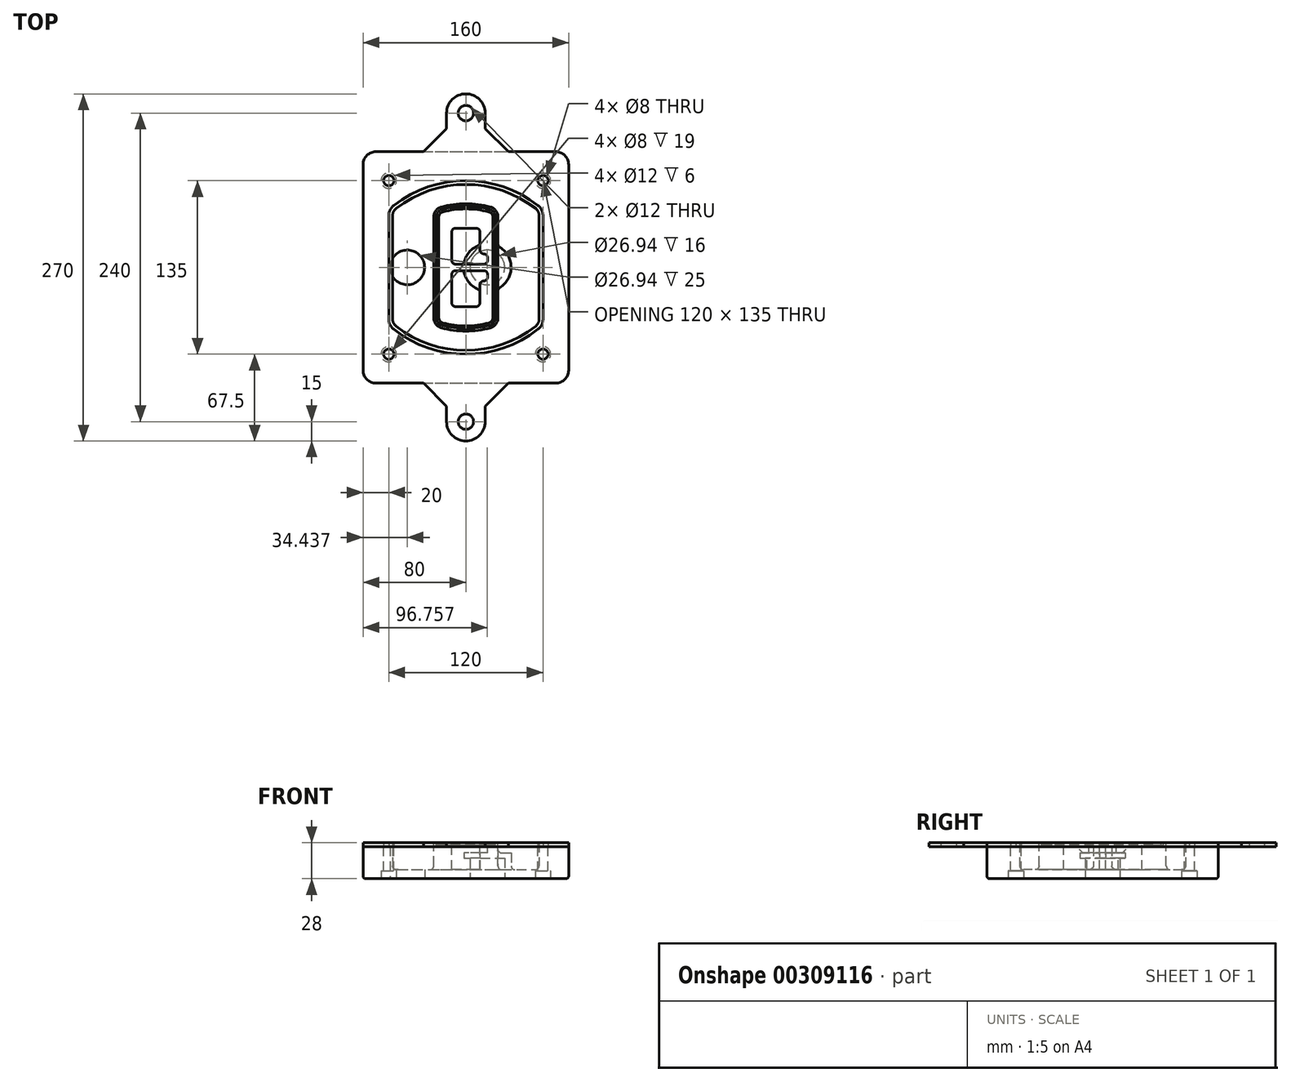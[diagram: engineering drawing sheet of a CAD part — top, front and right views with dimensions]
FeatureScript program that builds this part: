
annotation { "Feature Type Name" : "Feature", "Feature Type Description" : "" }
export const myFeature = defineFeature(function(context is Context, id is Id, definition is map)
    precondition{}
    {
        {
            var Q0;
            Q0=qCreatedBy(makeId("Top.planeOp"),FACE);
            var sketch = newSketch(context, id + "F0", { "sketchPlane" : qUnion([Q0])});
            skPoint(sketch, "E0.rect.middle", {"position": v(0, 0) * mm});
            skLineSegment(sketch, "E1.bottom", {"start": v(-70, -90) * mm, "end": v(70, -90) * mm});
            skLineSegment(sketch, "E1.top", {"start": v(-70, 90) * mm, "end": v(70, 90) * mm});
            skLineSegment(sketch, "E1.left", {"start": v(-80, -80) * mm, "end": v(-80, 80) * mm});
            skLineSegment(sketch, "E1.right", {"start": v(80, -80) * mm, "end": v(80, 80) * mm});
            skLineSegment(sketch, "E2", {"start": v(-80, 90) * mm, "end": v(80, -90) * mm, "construction": true});
            skLineSegment(sketch, "E3", {"start": v(80, 90) * mm, "end": v(-80, -90) * mm, "construction": true});
            skCircle(sketch, "E4", {"center": v(-60, 67.5) * mm, "radius": 4 * mm});
            skCircle(sketch, "E5", {"center": v(60, 67.5) * mm, "radius": 4 * mm});
            skCircle(sketch, "E6", {"center": v(60, -67.5) * mm, "radius": 4 * mm});
            skCircle(sketch, "E7", {"center": v(-60, -67.5) * mm, "radius": 4 * mm});
            skLineSegment(sketch, "E8", {"start": v(-60, 67.5) * mm, "end": v(60, 67.5) * mm, "construction": true});
            skLineSegment(sketch, "E9", {"start": v(60, 67.5) * mm, "end": v(60, -67.5) * mm, "construction": true});
            skLineSegment(sketch, "E10", {"start": v(60, -67.5) * mm, "end": v(-60, -67.5) * mm, "construction": true});
            skLineSegment(sketch, "E11", {"start": v(-60, -67.5) * mm, "end": v(-60, 67.5) * mm, "construction": true});
            skLineSegment(sketch, "E12", {"start": v(-60, 40.3) * mm, "end": v(-60, -40.3) * mm});
            skLineSegment(sketch, "E13", {"start": v(60, 40.3) * mm, "end": v(60, -40.3) * mm});
            skArc(sketch, "E14", {"start": v(56.15, 48.18) * mm, "mid": v(0, 67.5) * mm, "end": v(-56.15, 48.18) * mm});
            skArc(sketch, "E15", {"start": v(-56.15, -48.18) * mm, "mid": v(0, -67.5) * mm, "end": v(56.15, -48.18) * mm});
            skLineSegment(sketch, "E16", {"start": v(-60, 0) * mm, "end": v(60, 0) * mm, "construction": true});
            skPoint(sketch, "E17.visualSharp", {"position": v(-60, -45) * mm});
            skArc(sketch, "E17.filletArc", {"start": v(-60, -40.3) * mm, "mid": v(-58.99, -44.68) * mm, "end": v(-56.15, -48.18) * mm});
            skPoint(sketch, "E18.visualSharp", {"position": v(-60, 45) * mm});
            skArc(sketch, "E18.filletArc", {"start": v(-56.15, 48.18) * mm, "mid": v(-58.99, 44.68) * mm, "end": v(-60, 40.3) * mm});
            skPoint(sketch, "E19.visualSharp", {"position": v(60, 45) * mm});
            skArc(sketch, "E19.filletArc", {"start": v(60, 40.3) * mm, "mid": v(58.99, 44.68) * mm, "end": v(56.15, 48.18) * mm});
            skPoint(sketch, "E20.visualSharp", {"position": v(60, -45) * mm});
            skArc(sketch, "E20.filletArc", {"start": v(56.15, -48.18) * mm, "mid": v(58.99, -44.68) * mm, "end": v(60, -40.3) * mm});
            skPoint(sketch, "E21.visualSharp", {"position": v(-80, 90) * mm});
            skArc(sketch, "E21.filletArc", {"start": v(-70, 90) * mm, "mid": v(-77.07, 87.07) * mm, "end": v(-80, 80) * mm});
            skPoint(sketch, "E22.visualSharp", {"position": v(80, 90) * mm});
            skArc(sketch, "E22.filletArc", {"start": v(80, 80) * mm, "mid": v(77.07, 87.07) * mm, "end": v(70, 90) * mm});
            skPoint(sketch, "E23.visualSharp", {"position": v(80, -90) * mm});
            skArc(sketch, "E23.filletArc", {"start": v(70, -90) * mm, "mid": v(77.07, -87.07) * mm, "end": v(80, -80) * mm});
            skPoint(sketch, "E24.visualSharp", {"position": v(-80, -90) * mm});
            skArc(sketch, "E24.filletArc", {"start": v(-80, -80) * mm, "mid": v(-77.07, -87.07) * mm, "end": v(-70, -90) * mm});
            skArc(sketch, "E25.0", {"start": v(57, 40.3) * mm, "mid": v(56.3, 43.36) * mm, "end": v(54.3, 45.81) * mm});
            skLineSegment(sketch, "E25.1", {"start": v(57, 40.3) * mm, "end": v(57, -40.3) * mm});
            skArc(sketch, "E25.2", {"start": v(54.3, -45.81) * mm, "mid": v(56.3, -43.36) * mm, "end": v(57, -40.3) * mm});
            skArc(sketch, "E25.3", {"start": v(-54.3, -45.81) * mm, "mid": v(0, -64.5) * mm, "end": v(54.3, -45.81) * mm});
            skArc(sketch, "E25.4", {"start": v(-57, -40.3) * mm, "mid": v(-56.3, -43.36) * mm, "end": v(-54.3, -45.81) * mm});
            skArc(sketch, "E25.5", {"start": v(54.3, 45.81) * mm, "mid": v(0, 64.5) * mm, "end": v(-54.3, 45.81) * mm});
            skLineSegment(sketch, "E25.6", {"start": v(-57, 40.3) * mm, "end": v(-57, -40.3) * mm});
            skArc(sketch, "E25.7", {"start": v(-54.3, 45.81) * mm, "mid": v(-56.3, 43.36) * mm, "end": v(-57, 40.3) * mm});
            skArc(sketch, "E26.0", {"start": v(-58.62, 51.33) * mm, "mid": v(-62.58, 46.43) * mm, "end": v(-64, 40.3) * mm});
            skArc(sketch, "E26.1", {"start": v(58.62, 51.33) * mm, "mid": v(0, 71.5) * mm, "end": v(-58.62, 51.33) * mm});
            skArc(sketch, "E26.2", {"start": v(64, 40.3) * mm, "mid": v(62.58, 46.43) * mm, "end": v(58.62, 51.33) * mm});
            skLineSegment(sketch, "E26.3", {"start": v(64, 40.3) * mm, "end": v(64, -40.3) * mm});
            skArc(sketch, "E26.4", {"start": v(58.62, -51.33) * mm, "mid": v(62.58, -46.43) * mm, "end": v(64, -40.3) * mm});
            skLineSegment(sketch, "E26.5", {"start": v(-64, 40.3) * mm, "end": v(-64, -40.3) * mm});
            skArc(sketch, "E26.6", {"start": v(-58.62, -51.33) * mm, "mid": v(0, -71.5) * mm, "end": v(58.62, -51.33) * mm});
            skArc(sketch, "E26.7", {"start": v(-64, -40.3) * mm, "mid": v(-62.58, -46.43) * mm, "end": v(-58.62, -51.33) * mm});
            skSolve(sketch);
        }
        {
            var Q0;
            Q0=makeQuery(id+"F0.imprint","IMPRINT",FACE,{"disambiguationData":[TD([[makeQuery(id+"F0.imprint","IMPRINT",EDGE,{"derivedFrom":sQuery(id+"F0.wireOp",EDGE,"E1.bottom")}),1.0]])]});
            var Q1;
            Q1=makeQuery(id+"F0.imprint","IMPRINT",FACE,{"disambiguationData":[TD([[makeQuery(id+"F0.imprint","IMPRINT",EDGE,{"derivedFrom":sQuery(id+"F0.wireOp",EDGE,"E12")}),1.0]])]});
            var Q2;
            Q2=makeQuery(id+"F0.imprint","IMPRINT",FACE,{"disambiguationData":[TD([[makeQuery(id+"F0.imprint","IMPRINT",EDGE,{"derivedFrom":sQuery(id+"F0.wireOp",EDGE,"E25.0")}),1.0]])]});
            var Q3;
            Q3=makeQuery(id+"F0.imprint","IMPRINT",FACE,{"disambiguationData":[TD([[makeQuery(id+"F0.imprint","IMPRINT",EDGE,{"derivedFrom":sQuery(id+"F0.wireOp",EDGE,"E12")}),-1.0]])]});
            extrude(context, id + "F1", {"entities" : qUnion([Q0, Q1, Q2, Q3]), "oppositeDirection" : true, "depth" : 25 * mm});
        }
        {
            var Q0;
            Q0=makeQuery(id+"F0.imprint","IMPRINT",FACE,{"disambiguationData":[TD([[makeQuery(id+"F0.imprint","IMPRINT",EDGE,{"derivedFrom":sQuery(id+"F0.wireOp",EDGE,"E12")}),1.0]])]});
            extrude(context, id + "F2", {"entities" : qUnion([Q0]), "operationType" : NewBodyOperationType.ADD, "depth" : 3 * mm});
        }
        {
            var Q0;
            Q0=makeQuery(id+"F0.imprint","IMPRINT",FACE,{"disambiguationData":[TD([[makeQuery(id+"F0.imprint","IMPRINT",EDGE,{"derivedFrom":sQuery(id+"F0.wireOp",EDGE,"E25.0")}),1.0]])]});
            extrude(context, id + "F3", {"entities" : qUnion([Q0]), "operationType" : NewBodyOperationType.REMOVE, "oppositeDirection" : true, "depth" : 18 * mm});
        }
        {
            var Q0;
            Q0=makeQuery(id+"F2.opExtrude","CAP_FACE",FACE,{"disambiguationData":[OSD([sQuery(id+"F0.wireOp",EDGE,"E12"),sQuery(id+"F0.wireOp",EDGE,"E13"),sQuery(id+"F0.wireOp",EDGE,"E14"),sQuery(id+"F0.wireOp",EDGE,"E15"),sQuery(id+"F0.wireOp",EDGE,"E17.filletArc"),sQuery(id+"F0.wireOp",EDGE,"E18.filletArc"),sQuery(id+"F0.wireOp",EDGE,"E19.filletArc"),sQuery(id+"F0.wireOp",EDGE,"E20.filletArc"),sQuery(id+"F0.wireOp",EDGE,"E25.0"),sQuery(id+"F0.wireOp",EDGE,"E25.1"),sQuery(id+"F0.wireOp",EDGE,"E25.2"),sQuery(id+"F0.wireOp",EDGE,"E25.3"),sQuery(id+"F0.wireOp",EDGE,"E25.4"),sQuery(id+"F0.wireOp",EDGE,"E25.5"),sQuery(id+"F0.wireOp",EDGE,"E25.6"),sQuery(id+"F0.wireOp",EDGE,"E25.7")])],"isStart":false});
            var sketch = newSketch(context, id + "F4", { "sketchPlane" : qUnion([Q0])});
            skArc(sketch, "E27.0", {"start": v(-19.08, -46.97) * mm, "mid": v(0, -49.5) * mm, "end": v(19.08, -46.97) * mm});
            skArc(sketch, "E28.0", {"start": v(19.08, 46.97) * mm, "mid": v(0, 49.5) * mm, "end": v(-19.08, 46.97) * mm});
            skLineSegment(sketch, "E29", {"start": v(-25, 39.25) * mm, "end": v(-25, -39.25) * mm});
            skLineSegment(sketch, "E30", {"start": v(25, 39.25) * mm, "end": v(25, -39.25) * mm});
            skLineSegment(sketch, "E31", {"start": v(-25, 45.1) * mm, "end": v(25, 45.1) * mm, "construction": true});
            skLineSegment(sketch, "E32", {"start": v(-25, -45.1) * mm, "end": v(25, -45.1) * mm, "construction": true});
            skPoint(sketch, "E33.visualSharp", {"position": v(-25, 45.1) * mm});
            skArc(sketch, "E33.filletArc", {"start": v(-19.08, 46.97) * mm, "mid": v(-23.35, 44.11) * mm, "end": v(-25, 39.25) * mm});
            skPoint(sketch, "E34.visualSharp", {"position": v(25, 45.1) * mm});
            skArc(sketch, "E34.filletArc", {"start": v(25, 39.25) * mm, "mid": v(23.35, 44.11) * mm, "end": v(19.08, 46.97) * mm});
            skPoint(sketch, "E35.visualSharp", {"position": v(25, -45.1) * mm});
            skArc(sketch, "E35.filletArc", {"start": v(19.08, -46.97) * mm, "mid": v(23.35, -44.11) * mm, "end": v(25, -39.25) * mm});
            skPoint(sketch, "E36.visualSharp", {"position": v(-25, -45.1) * mm});
            skArc(sketch, "E36.filletArc", {"start": v(-25, -39.25) * mm, "mid": v(-23.35, -44.11) * mm, "end": v(-19.08, -46.97) * mm});
            skArc(sketch, "E37.0", {"start": v(54.3, 45.81) * mm, "mid": v(0, 64.5) * mm, "end": v(-54.3, 45.81) * mm});
            skArc(sketch, "E37.1", {"start": v(-54.3, 45.81) * mm, "mid": v(-56.3, 43.36) * mm, "end": v(-57, 40.3) * mm});
            skLineSegment(sketch, "E37.2", {"start": v(-57, 40.3) * mm, "end": v(-57, -40.3) * mm});
            skArc(sketch, "E37.3", {"start": v(-57, -40.3) * mm, "mid": v(-56.3, -43.36) * mm, "end": v(-54.3, -45.81) * mm});
            skArc(sketch, "E37.4", {"start": v(-54.3, -45.81) * mm, "mid": v(0, -64.5) * mm, "end": v(54.3, -45.81) * mm});
            skArc(sketch, "E37.5", {"start": v(54.3, -45.81) * mm, "mid": v(56.3, -43.36) * mm, "end": v(57, -40.3) * mm});
            skLineSegment(sketch, "E37.6", {"start": v(57, 40.3) * mm, "end": v(57, -40.3) * mm});
            skArc(sketch, "E37.7", {"start": v(57, 40.3) * mm, "mid": v(56.3, 43.36) * mm, "end": v(54.3, 45.81) * mm});
            skLineSegment(sketch, "E38.0", {"start": v(23, 39.25) * mm, "end": v(23, -39.25) * mm});
            skArc(sketch, "E38.1", {"start": v(18.56, -45.04) * mm, "mid": v(21.76, -42.9) * mm, "end": v(23, -39.25) * mm});
            skArc(sketch, "E38.2", {"start": v(-18.56, -45.04) * mm, "mid": v(0, -47.5) * mm, "end": v(18.56, -45.04) * mm});
            skArc(sketch, "E38.3", {"start": v(-23, -39.25) * mm, "mid": v(-21.76, -42.9) * mm, "end": v(-18.56, -45.04) * mm});
            skLineSegment(sketch, "E38.4", {"start": v(-23, 39.25) * mm, "end": v(-23, -39.25) * mm});
            skArc(sketch, "E38.5", {"start": v(23, 39.25) * mm, "mid": v(21.76, 42.9) * mm, "end": v(18.56, 45.04) * mm});
            skArc(sketch, "E38.6", {"start": v(-18.56, 45.04) * mm, "mid": v(-21.76, 42.9) * mm, "end": v(-23, 39.25) * mm});
            skArc(sketch, "E38.7", {"start": v(18.56, 45.04) * mm, "mid": v(0, 47.5) * mm, "end": v(-18.56, 45.04) * mm});
            skArc(sketch, "E39.0", {"start": v(21, 39.25) * mm, "mid": v(20.18, 41.68) * mm, "end": v(18.04, 43.1) * mm});
            skLineSegment(sketch, "E39.1", {"start": v(21, 39.25) * mm, "end": v(21, -39.25) * mm});
            skArc(sketch, "E39.2", {"start": v(18.04, -43.1) * mm, "mid": v(20.18, -41.68) * mm, "end": v(21, -39.25) * mm});
            skArc(sketch, "E39.3", {"start": v(-18.04, -43.1) * mm, "mid": v(0, -45.5) * mm, "end": v(18.04, -43.1) * mm});
            skArc(sketch, "E39.4", {"start": v(-21, -39.25) * mm, "mid": v(-20.18, -41.68) * mm, "end": v(-18.04, -43.1) * mm});
            skArc(sketch, "E39.5", {"start": v(18.04, 43.1) * mm, "mid": v(0, 45.5) * mm, "end": v(-18.04, 43.1) * mm});
            skLineSegment(sketch, "E39.6", {"start": v(-21, 39.25) * mm, "end": v(-21, -39.25) * mm});
            skArc(sketch, "E39.7", {"start": v(-18.04, 43.1) * mm, "mid": v(-20.18, 41.68) * mm, "end": v(-21, 39.25) * mm});
            skLineSegment(sketch, "E40", {"start": v(-25, 0) * mm, "end": v(25, 0) * mm, "construction": true});
            skLineSegment(sketch, "E41", {"start": v(-11, 5.5) * mm, "end": v(-11, 27.5) * mm});
            skLineSegment(sketch, "E42", {"start": v(-8, 30.5) * mm, "end": v(8, 30.5) * mm});
            skLineSegment(sketch, "E43", {"start": v(11, 27.5) * mm, "end": v(11, 13.5) * mm});
            skLineSegment(sketch, "E44", {"start": v(14, 10.5) * mm, "end": v(14, 10.5) * mm});
            skLineSegment(sketch, "E45", {"start": v(17, 7.5) * mm, "end": v(17, 5.5) * mm});
            skLineSegment(sketch, "E46", {"start": v(14, 2.5) * mm, "end": v(-8, 2.5) * mm});
            skPoint(sketch, "E47.visualSharp", {"position": v(-11, 30.5) * mm});
            skArc(sketch, "E47.filletArc", {"start": v(-8, 30.5) * mm, "mid": v(-10.12, 29.62) * mm, "end": v(-11, 27.5) * mm});
            skPoint(sketch, "E48.visualSharp", {"position": v(11, 30.5) * mm});
            skArc(sketch, "E48.filletArc", {"start": v(11, 27.5) * mm, "mid": v(10.12, 29.62) * mm, "end": v(8, 30.5) * mm});
            skPoint(sketch, "E49.visualSharp", {"position": v(11, 10.5) * mm});
            skArc(sketch, "E49.filletArc", {"start": v(11, 13.5) * mm, "mid": v(11.88, 11.38) * mm, "end": v(14, 10.5) * mm});
            skPoint(sketch, "E50.visualSharp", {"position": v(17, 10.5) * mm});
            skArc(sketch, "E50.filletArc", {"start": v(17, 7.5) * mm, "mid": v(16.12, 9.62) * mm, "end": v(14, 10.5) * mm});
            skPoint(sketch, "E51.visualSharp", {"position": v(17, 2.5) * mm});
            skArc(sketch, "E51.filletArc", {"start": v(14, 2.5) * mm, "mid": v(16.12, 3.38) * mm, "end": v(17, 5.5) * mm});
            skPoint(sketch, "E52.visualSharp", {"position": v(-11, 2.5) * mm});
            skArc(sketch, "E52.filletArc", {"start": v(-11, 5.5) * mm, "mid": v(-10.12, 3.38) * mm, "end": v(-8, 2.5) * mm});
            skLineSegment(sketch, "E53.0.MirrorCS", {"start": v(14, -2.5) * mm, "end": v(-8, -2.5) * mm});
            skArc(sketch, "E54.0.MirrorCS", {"start": v(-11, -5.5) * mm, "mid": v(-10.12, -3.38) * mm, "end": v(-8, -2.5) * mm});
            skLineSegment(sketch, "E55.0.MirrorCS", {"start": v(-11, -5.5) * mm, "end": v(-11, -27.5) * mm});
            skArc(sketch, "E56.0.MirrorCS", {"start": v(-8, -30.5) * mm, "mid": v(-10.12, -29.62) * mm, "end": v(-11, -27.5) * mm});
            skLineSegment(sketch, "E57.0.MirrorCS", {"start": v(-8, -30.5) * mm, "end": v(8, -30.5) * mm});
            skArc(sketch, "E58.0.MirrorCS", {"start": v(11, -27.5) * mm, "mid": v(10.12, -29.62) * mm, "end": v(8, -30.5) * mm});
            skLineSegment(sketch, "E59.0.MirrorCS", {"start": v(11, -27.5) * mm, "end": v(11, -13.5) * mm});
            skArc(sketch, "E60.0.MirrorCS", {"start": v(11, -13.5) * mm, "mid": v(11.88, -11.38) * mm, "end": v(14, -10.5) * mm});
            skArc(sketch, "E61.0.MirrorCS", {"start": v(17, -7.5) * mm, "mid": v(16.12, -9.62) * mm, "end": v(14, -10.5) * mm});
            skLineSegment(sketch, "E62.0.MirrorCS", {"start": v(17, -7.5) * mm, "end": v(17, -5.5) * mm});
            skArc(sketch, "E63.0.MirrorCS", {"start": v(14, -2.5) * mm, "mid": v(16.12, -3.38) * mm, "end": v(17, -5.5) * mm});
            skSolve(sketch);
        }
        {
            var Q0;
            Q0=makeQuery(id+"F4.imprint","IMPRINT",FACE,{"disambiguationData":[TD([[makeQuery(id+"F4.imprint","IMPRINT",EDGE,{"derivedFrom":sQuery(id+"F4.wireOp",EDGE,"E27.0")}),1.0]])]});
            var Q1;
            Q1=makeQuery(id+"F4.imprint","IMPRINT",FACE,{"disambiguationData":[TD([[makeQuery(id+"F4.imprint","IMPRINT",EDGE,{"derivedFrom":sQuery(id+"F4.wireOp",EDGE,"E38.0")}),-1.0]])]});
            var Q2;
            Q2=makeQuery(id+"F4.imprint","IMPRINT",FACE,{"disambiguationData":[TD([[makeQuery(id+"F4.imprint","IMPRINT",EDGE,{"derivedFrom":sQuery(id+"F4.wireOp",EDGE,"E39.0")}),1.0]])]});
            extrude(context, id + "F5", {"entities" : qUnion([Q0, Q1, Q2]), "operationType" : NewBodyOperationType.ADD, "endBound" : BoundingType.UP_TO_NEXT, "oppositeDirection" : true, "depth" : 25 * mm});
        }
        {
            var Q0;
            Q0=makeQuery(id+"F4.imprint","IMPRINT",FACE,{"disambiguationData":[TD([[makeQuery(id+"F4.imprint","IMPRINT",EDGE,{"derivedFrom":sQuery(id+"F4.wireOp",EDGE,"E38.0")}),-1.0]])]});
            extrude(context, id + "F6", {"entities" : qUnion([Q0]), "operationType" : NewBodyOperationType.REMOVE, "oppositeDirection" : true, "depth" : 2 * mm});
        }
        {
            var Q0;
            Q0=makeQuery(id+"F1.opExtrude","CAP_FACE",FACE,{"disambiguationData":[OSD([sQuery(id+"F0.wireOp",EDGE,"E1.bottom"),sQuery(id+"F0.wireOp",EDGE,"E1.top"),sQuery(id+"F0.wireOp",EDGE,"E1.left"),sQuery(id+"F0.wireOp",EDGE,"E1.right"),sQuery(id+"F0.wireOp",EDGE,"E4"),sQuery(id+"F0.wireOp",EDGE,"E5"),sQuery(id+"F0.wireOp",EDGE,"E6"),sQuery(id+"F0.wireOp",EDGE,"E7"),sQuery(id+"F0.wireOp",EDGE,"E21.filletArc"),sQuery(id+"F0.wireOp",EDGE,"E22.filletArc"),sQuery(id+"F0.wireOp",EDGE,"E23.filletArc"),sQuery(id+"F0.wireOp",EDGE,"E24.filletArc")])],"isStart":false});
            var sketch = newSketch(context, id + "F7", { "sketchPlane" : qUnion([Q0])});
            skCircle(sketch, "E64", {"center": v(16.76, 0) * mm, "radius": 13.47 * mm});
            skCircle(sketch, "E65", {"center": v(-45.56, 0) * mm, "radius": 13.47 * mm});
            skLineSegment(sketch, "E66", {"start": v(80, 0) * mm, "end": v(-80, 0) * mm});
            skCircle(sketch, "E67", {"center": v(16.76, 0) * mm, "radius": 18.47 * mm});
            skCircle(sketch, "E68", {"center": v(60, -67.5) * mm, "radius": 6 * mm});
            skCircle(sketch, "E69", {"center": v(-60, -67.5) * mm, "radius": 6 * mm});
            skCircle(sketch, "E70", {"center": v(-60, 67.5) * mm, "radius": 6 * mm});
            skCircle(sketch, "E71", {"center": v(60, 67.5) * mm, "radius": 6 * mm});
            skSolve(sketch);
        }
        {
            var Q0;
            {var subQ1=sQuery(id+"F7.wireOp",EDGE,"E66");var subQ4=sQuery(id+"F7.wireOp",EDGE,"E64");var subQ6=makeQuery(id+"F7.imprint","INTERSECT",VERTEX,{"disambiguationData":[OD(0.0)],"derivedFrom":[subQ4,subQ1]});Q0=makeQuery(id+"F7.imprint","IMPRINT",FACE,{"disambiguationData":[TD([[makeQuery(id+"F7.imprint","IMPRINT",EDGE,{"disambiguationData":[TD([[subQ6,-1.0]])],"derivedFrom":subQ4}),-1.0]])]});}
            var Q1;
            {var subQ0=sQuery(id+"F7.wireOp",EDGE,"E66");var subQ1=sQuery(id+"F7.wireOp",EDGE,"E64");var subQ3=makeQuery(id+"F7.imprint","INTERSECT",VERTEX,{"disambiguationData":[OD(0.0)],"derivedFrom":[subQ1,subQ0]});Q1=makeQuery(id+"F7.imprint","IMPRINT",FACE,{"disambiguationData":[TD([[makeQuery(id+"F7.imprint","IMPRINT",EDGE,{"disambiguationData":[TD([[subQ3,-1.0]])],"derivedFrom":subQ1}),1.0]])]});}
            var Q2;
            {var subQ0=sQuery(id+"F7.wireOp",EDGE,"E66");var subQ1=sQuery(id+"F7.wireOp",EDGE,"E64");var subQ3=makeQuery(id+"F7.imprint","INTERSECT",VERTEX,{"disambiguationData":[OD(0.0)],"derivedFrom":[subQ1,subQ0]});Q2=makeQuery(id+"F7.imprint","IMPRINT",FACE,{"disambiguationData":[TD([[makeQuery(id+"F7.imprint","IMPRINT",EDGE,{"disambiguationData":[TD([[subQ3,1.0]])],"derivedFrom":subQ1}),1.0]])]});}
            var Q3;
            {var subQ1=sQuery(id+"F7.wireOp",EDGE,"E66");var subQ4=sQuery(id+"F7.wireOp",EDGE,"E64");var subQ6=makeQuery(id+"F7.imprint","INTERSECT",VERTEX,{"disambiguationData":[OD(0.0)],"derivedFrom":[subQ4,subQ1]});Q3=makeQuery(id+"F7.imprint","IMPRINT",FACE,{"disambiguationData":[TD([[makeQuery(id+"F7.imprint","IMPRINT",EDGE,{"disambiguationData":[TD([[subQ6,1.0]])],"derivedFrom":subQ4}),-1.0]])]});}
            extrude(context, id + "F8", {"entities" : qUnion([Q0, Q1, Q2, Q3]), "operationType" : NewBodyOperationType.ADD, "oppositeDirection" : true, "depth" : 20 * mm});
        }
        {
            var Q0;
            {var subQ0=sQuery(id+"F7.wireOp",EDGE,"E66");var subQ1=sQuery(id+"F7.wireOp",EDGE,"E64");var subQ3=makeQuery(id+"F7.imprint","INTERSECT",VERTEX,{"disambiguationData":[OD(0.0)],"derivedFrom":[subQ1,subQ0]});Q0=makeQuery(id+"F7.imprint","IMPRINT",FACE,{"disambiguationData":[TD([[makeQuery(id+"F7.imprint","IMPRINT",EDGE,{"disambiguationData":[TD([[subQ3,-1.0]])],"derivedFrom":subQ1}),1.0]])]});}
            var Q1;
            {var subQ0=sQuery(id+"F7.wireOp",EDGE,"E66");var subQ1=sQuery(id+"F7.wireOp",EDGE,"E64");var subQ3=makeQuery(id+"F7.imprint","INTERSECT",VERTEX,{"disambiguationData":[OD(0.0)],"derivedFrom":[subQ1,subQ0]});Q1=makeQuery(id+"F7.imprint","IMPRINT",FACE,{"disambiguationData":[TD([[makeQuery(id+"F7.imprint","IMPRINT",EDGE,{"disambiguationData":[TD([[subQ3,1.0]])],"derivedFrom":subQ1}),1.0]])]});}
            extrude(context, id + "F9", {"entities" : qUnion([Q0, Q1]), "operationType" : NewBodyOperationType.REMOVE, "oppositeDirection" : true, "depth" : 16 * mm});
        }
        {
            var Q0;
            {var subQ0=sQuery(id+"F7.wireOp",EDGE,"E66");var subQ1=sQuery(id+"F7.wireOp",EDGE,"E65");var subQ3=makeQuery(id+"F7.imprint","INTERSECT",VERTEX,{"disambiguationData":[OD(0.0)],"derivedFrom":[subQ1,subQ0]});Q0=makeQuery(id+"F7.imprint","IMPRINT",FACE,{"disambiguationData":[TD([[makeQuery(id+"F7.imprint","IMPRINT",EDGE,{"disambiguationData":[TD([[subQ3,-1.0]])],"derivedFrom":subQ1}),1.0]])]});}
            var Q1;
            {var subQ0=sQuery(id+"F7.wireOp",EDGE,"E66");var subQ1=sQuery(id+"F7.wireOp",EDGE,"E65");var subQ3=makeQuery(id+"F7.imprint","INTERSECT",VERTEX,{"disambiguationData":[OD(0.0)],"derivedFrom":[subQ1,subQ0]});Q1=makeQuery(id+"F7.imprint","IMPRINT",FACE,{"disambiguationData":[TD([[makeQuery(id+"F7.imprint","IMPRINT",EDGE,{"disambiguationData":[TD([[subQ3,1.0]])],"derivedFrom":subQ1}),1.0]])]});}
            extrude(context, id + "F10", {"entities" : qUnion([Q0, Q1]), "operationType" : NewBodyOperationType.REMOVE, "oppositeDirection" : true, "depth" : 25 * mm});
        }
        {
            var Q0;
            Q0=makeQuery(id+"F7.imprint","IMPRINT",FACE,{"disambiguationData":[TD([[makeQuery(id+"F7.imprint","IMPRINT",EDGE,{"derivedFrom":sQuery(id+"F7.wireOp",EDGE,"E68")}),1.0]])]});
            var Q1;
            Q1=makeQuery(id+"F7.imprint","IMPRINT",FACE,{"disambiguationData":[TD([[makeQuery(id+"F7.imprint","IMPRINT",EDGE,{"derivedFrom":makeQuery(id+"F1.opExtrude","CAP_EDGE",EDGE,{"disambiguationData":[OSD([sQuery(id+"F0.wireOp",EDGE,"E5")])],"isStart":false})}),-1.0]])]});
            var Q2;
            Q2=makeQuery(id+"F7.imprint","IMPRINT",FACE,{"disambiguationData":[TD([[makeQuery(id+"F7.imprint","IMPRINT",EDGE,{"derivedFrom":sQuery(id+"F7.wireOp",EDGE,"E69")}),1.0]])]});
            var Q3;
            Q3=makeQuery(id+"F7.imprint","IMPRINT",FACE,{"disambiguationData":[TD([[makeQuery(id+"F7.imprint","IMPRINT",EDGE,{"derivedFrom":makeQuery(id+"F1.opExtrude","CAP_EDGE",EDGE,{"disambiguationData":[OSD([sQuery(id+"F0.wireOp",EDGE,"E4")])],"isStart":false})}),-1.0]])]});
            var Q4;
            Q4=makeQuery(id+"F7.imprint","IMPRINT",FACE,{"disambiguationData":[TD([[makeQuery(id+"F7.imprint","IMPRINT",EDGE,{"derivedFrom":sQuery(id+"F7.wireOp",EDGE,"E70")}),1.0]])]});
            var Q5;
            Q5=makeQuery(id+"F7.imprint","IMPRINT",FACE,{"disambiguationData":[TD([[makeQuery(id+"F7.imprint","IMPRINT",EDGE,{"derivedFrom":makeQuery(id+"F1.opExtrude","CAP_EDGE",EDGE,{"disambiguationData":[OSD([sQuery(id+"F0.wireOp",EDGE,"E7")])],"isStart":false})}),-1.0]])]});
            var Q6;
            Q6=makeQuery(id+"F7.imprint","IMPRINT",FACE,{"disambiguationData":[TD([[makeQuery(id+"F7.imprint","IMPRINT",EDGE,{"derivedFrom":sQuery(id+"F7.wireOp",EDGE,"E71")}),1.0]])]});
            var Q7;
            Q7=makeQuery(id+"F7.imprint","IMPRINT",FACE,{"disambiguationData":[TD([[makeQuery(id+"F7.imprint","IMPRINT",EDGE,{"derivedFrom":makeQuery(id+"F1.opExtrude","CAP_EDGE",EDGE,{"disambiguationData":[OSD([sQuery(id+"F0.wireOp",EDGE,"E6")])],"isStart":false})}),-1.0]])]});
            extrude(context, id + "F11", {"entities" : qUnion([Q0, Q1, Q2, Q3, Q4, Q5, Q6, Q7]), "operationType" : NewBodyOperationType.REMOVE, "oppositeDirection" : true, "depth" : 6 * mm});
        }
        {
            var Q0;
            Q0=makeQuery(id+"F9.boolean.opBoolean","COPY",FACE,{"derivedFrom":makeQuery(id+"F9.opExtrude","CAP_FACE",FACE,{"disambiguationData":[OSD([sQuery(id+"F7.wireOp",EDGE,"E64")])],"isStart":false})});
            var sketch = newSketch(context, id + "F12", { "sketchPlane" : qUnion([Q0])});
            skArc(sketch, "E72.0", {"start": v(11, 17.55) * mm, "mid": v(2.57, 11.82) * mm, "end": v(-1.54, 2.5) * mm});
            skArc(sketch, "E72.1", {"start": v(-1.54, -2.5) * mm, "mid": v(2.57, -11.82) * mm, "end": v(11, -17.55) * mm});
            skLineSegment(sketch, "E73", {"start": v(-1.54, -2.5) * mm, "end": v(14, -2.5) * mm});
            skLineSegment(sketch, "E74.0", {"start": v(14, 2.5) * mm, "end": v(-1.54, 2.5) * mm});
            skArc(sketch, "E74.1", {"start": v(14, 2.5) * mm, "mid": v(16.12, 3.38) * mm, "end": v(17, 5.5) * mm});
            skLineSegment(sketch, "E74.2", {"start": v(17, 7.5) * mm, "end": v(17, 5.5) * mm});
            skArc(sketch, "E74.3", {"start": v(17, 7.5) * mm, "mid": v(16.12, 9.62) * mm, "end": v(14, 10.5) * mm});
            skArc(sketch, "E74.4", {"start": v(11, 13.5) * mm, "mid": v(11.88, 11.38) * mm, "end": v(14, 10.5) * mm});
            skLineSegment(sketch, "E74.5", {"start": v(11, 17.55) * mm, "end": v(11, 13.5) * mm});
            skLineSegment(sketch, "E74.7", {"start": v(14, -2.5) * mm, "end": v(-1.54, -2.5) * mm});
            skArc(sketch, "E74.8", {"start": v(14, -2.5) * mm, "mid": v(16.12, -3.38) * mm, "end": v(17, -5.5) * mm});
            skLineSegment(sketch, "E74.9", {"start": v(17, -7.5) * mm, "end": v(17, -5.5) * mm});
            skArc(sketch, "E74.10", {"start": v(17, -7.5) * mm, "mid": v(16.12, -9.62) * mm, "end": v(14, -10.5) * mm});
            skArc(sketch, "E74.11", {"start": v(11, -13.5) * mm, "mid": v(11.88, -11.38) * mm, "end": v(14, -10.5) * mm});
            skLineSegment(sketch, "E74.12", {"start": v(11, -17.55) * mm, "end": v(11, -13.5) * mm});
            skPoint(sketch, "E75.orphan", {"position": v(11, -27.5) * mm});
            skPoint(sketch, "E76.orphan", {"position": v(-8, -2.5) * mm});
            skPoint(sketch, "E77.orphan", {"position": v(-8, 2.5) * mm});
            skPoint(sketch, "E78.orphan", {"position": v(11, 27.5) * mm});
            skSolve(sketch);
        }
        {
            var Q0;
            {var subQ7=sQuery(id+"F12.wireOp",EDGE,"E72.0");var subQ14=sQuery(id+"F12.wireOp",EDGE,"E72.1");var subQ16=sQuery(id+"F12.wireOp",EDGE,"E74.1");var subQ18=sQuery(id+"F12.wireOp",EDGE,"E74.8");Q0=qUnion([makeQuery(id+"F12.imprint","IMPRINT",FACE,{"disambiguationData":[TD([[makeQuery(id+"F12.imprint","IMPRINT",EDGE,{"derivedFrom":subQ7}),1.0]])]}),makeQuery(id+"F12.imprint","IMPRINT",FACE,{"disambiguationData":[TD([[makeQuery(id+"F12.imprint","IMPRINT",EDGE,{"derivedFrom":subQ14}),1.0]])]}),makeQuery(id+"F12.imprint","IMPRINT",FACE,{"disambiguationData":[TD([[makeQuery(id+"F12.imprint","IMPRINT",EDGE,{"derivedFrom":subQ16}),1.0]])]}),makeQuery(id+"F12.imprint","IMPRINT",FACE,{"disambiguationData":[TD([[makeQuery(id+"F12.imprint","IMPRINT",EDGE,{"derivedFrom":subQ18}),-1.0]])]})]);}
            var Q1;
            Q1=makeQuery(id+"F5.boolean.opBoolean","SPLIT",FACE,{"disambiguationData":[TD([makeQuery(id+"F5.opExtrude","SWEPT_FACE",FACE,{"disambiguationData":[OSD([sQuery(id+"F4.wireOp",EDGE,"E41")])]})])],"derivedFrom":makeQuery(id+"F3.boolean.opBoolean","COPY",FACE,{"derivedFrom":makeQuery(id+"F3.opExtrude","CAP_FACE",FACE,{"disambiguationData":[OSD([sQuery(id+"F0.wireOp",EDGE,"E25.0"),sQuery(id+"F0.wireOp",EDGE,"E25.1"),sQuery(id+"F0.wireOp",EDGE,"E25.2"),sQuery(id+"F0.wireOp",EDGE,"E25.3"),sQuery(id+"F0.wireOp",EDGE,"E25.4"),sQuery(id+"F0.wireOp",EDGE,"E25.5"),sQuery(id+"F0.wireOp",EDGE,"E25.6"),sQuery(id+"F0.wireOp",EDGE,"E25.7")])],"isStart":false})})});
            extrude(context, id + "F13", {"entities" : qUnion([Q0]), "operationType" : NewBodyOperationType.REMOVE, "endBound" : BoundingType.UP_TO_SURFACE, "endBoundEntityFace" : qUnion([Q1]), "depth" : 25 * mm});
        }
        {
            var Q0;
            Q0=makeQuery(id+"F3.boolean.opBoolean","COPY",EDGE,{"derivedFrom":makeQuery(id+"F3.opExtrude","CAP_EDGE",EDGE,{"disambiguationData":[OSD([sQuery(id+"F0.wireOp",EDGE,"E25.6")])],"isStart":false})});
            var Q1;
            Q1=makeQuery(id+"F8.boolean.opBoolean","INTERSECT",EDGE,{"derivedFrom":[makeQuery(id+"F5.opExtrude","SWEPT_FACE",FACE,{"disambiguationData":[OSD([sQuery(id+"F4.wireOp",EDGE,"E30")])]}),makeQuery(id+"F8.opExtrude","CAP_FACE",FACE,{"disambiguationData":[OSD([sQuery(id+"F7.wireOp",EDGE,"E67")])],"isStart":false})]});
            var Q2;
            Q2=makeQuery(id+"F8.boolean.opBoolean","INTERSECT",EDGE,{"disambiguationData":[OD(1.0)],"derivedFrom":[makeQuery(id+"F5.opExtrude","SWEPT_FACE",FACE,{"disambiguationData":[OSD([sQuery(id+"F4.wireOp",EDGE,"E30")])]}),makeQuery(id+"F8.opExtrude","SWEPT_FACE",FACE,{"disambiguationData":[OSD([sQuery(id+"F7.wireOp",EDGE,"E67")])]})]});
            var Q3;
            {var subQ0=sQuery(id+"F4.wireOp",EDGE,"E30");Q3=makeQuery(id+"F8.boolean.opBoolean","SPLIT",EDGE,{"disambiguationData":[TD([makeQuery(id+"F5.opExtrude","SWEPT_FACE",FACE,{"disambiguationData":[OSD([sQuery(id+"F4.wireOp",EDGE,"E35.filletArc")])]})])],"derivedFrom":makeQuery(id+"F5.opExtrude","CAP_EDGE",EDGE,{"disambiguationData":[OSD([subQ0])],"isStart":false})});}
            var Q4;
            {var subQ0=sQuery(id+"F0.wireOp",EDGE,"E25.7");var subQ1=sQuery(id+"F0.wireOp",EDGE,"E25.1");var subQ2=sQuery(id+"F0.wireOp",EDGE,"E25.6");var subQ3=sQuery(id+"F0.wireOp",EDGE,"E25.5");var subQ4=sQuery(id+"F0.wireOp",EDGE,"E25.4");var subQ5=sQuery(id+"F0.wireOp",EDGE,"E25.0");var subQ6=sQuery(id+"F0.wireOp",EDGE,"E25.2");var subQ7=sQuery(id+"F0.wireOp",EDGE,"E25.3");Q4=makeQuery(id+"F8.boolean.opBoolean","INTERSECT",EDGE,{"derivedFrom":[makeQuery(id+"F5.boolean.opBoolean","SPLIT",FACE,{"disambiguationData":[TD([makeQuery(id+"F2.opExtrude","SWEPT_FACE",FACE,{"disambiguationData":[OSD([subQ5])]})])],"derivedFrom":makeQuery(id+"F3.boolean.opBoolean","COPY",FACE,{"derivedFrom":makeQuery(id+"F3.opExtrude","CAP_FACE",FACE,{"disambiguationData":[OSD([subQ5,subQ1,subQ6,subQ7,subQ4,subQ3,subQ2,subQ0])],"isStart":false})})}),makeQuery(id+"F8.opExtrude","SWEPT_FACE",FACE,{"disambiguationData":[OSD([sQuery(id+"F7.wireOp",EDGE,"E67")])]})]});}
            var Q5;
            Q5=makeQuery(id+"F8.boolean.opBoolean","INTERSECT",EDGE,{"disambiguationData":[OD(0.0)],"derivedFrom":[makeQuery(id+"F5.opExtrude","SWEPT_FACE",FACE,{"disambiguationData":[OSD([sQuery(id+"F4.wireOp",EDGE,"E30")])]}),makeQuery(id+"F8.opExtrude","SWEPT_FACE",FACE,{"disambiguationData":[OSD([sQuery(id+"F7.wireOp",EDGE,"E67")])]})]});
            fillet(context, id + "F14", {"entities" : qUnion([Q0, Q1, Q2, Q3, Q4, Q5]), "radius" : 3 * mm, "tangentPropagation" : true, "allowEdgeOverflow" : false});
        }
        {
            var Q0;
            Q0=makeQuery(id+"F1.opExtrude","CAP_EDGE",EDGE,{"disambiguationData":[OSD([sQuery(id+"F0.wireOp",EDGE,"E1.bottom")])],"isStart":false});
            fillet(context, id + "F15", {"entities" : qUnion([Q0]), "radius" : 2 * mm, "tangentPropagation" : true, "allowEdgeOverflow" : false});
        }
        {
            var Q0;
            {var subQ0=sQuery(id+"F0.wireOp",EDGE,"E21.filletArc");var subQ1=sQuery(id+"F0.wireOp",EDGE,"E7");var subQ2=sQuery(id+"F0.wireOp",EDGE,"E6");var subQ3=sQuery(id+"F0.wireOp",EDGE,"E5");var subQ4=sQuery(id+"F0.wireOp",EDGE,"E4");var subQ5=sQuery(id+"F0.wireOp",EDGE,"E22.filletArc");var subQ6=sQuery(id+"F0.wireOp",EDGE,"E1.bottom");var subQ7=sQuery(id+"F0.wireOp",EDGE,"E1.right");var subQ8=sQuery(id+"F0.wireOp",EDGE,"E1.top");var subQ9=sQuery(id+"F0.wireOp",EDGE,"E1.left");var subQ10=sQuery(id+"F0.wireOp",EDGE,"E23.filletArc");var subQ11=sQuery(id+"F0.wireOp",EDGE,"E24.filletArc");Q0=makeQuery(id+"F2.boolean.opBoolean","SPLIT",FACE,{"disambiguationData":[TD([makeQuery(id+"F1.opExtrude","SWEPT_FACE",FACE,{"disambiguationData":[OSD([subQ6])]})])],"derivedFrom":makeQuery(id+"F1.opExtrude","CAP_FACE",FACE,{"disambiguationData":[OSD([subQ6,subQ8,subQ9,subQ7,subQ4,subQ3,subQ2,subQ1,subQ0,subQ5,subQ10,subQ11])],"isStart":true})});}
            var sketch = newSketch(context, id + "F16", { "sketchPlane" : qUnion([Q0])});
            skLineSegment(sketch, "E79", {"start": v(0, 90) * mm, "end": v(0, 120) * mm, "construction": true});
            skCircle(sketch, "E80", {"center": v(0, 120) * mm, "radius": 6 * mm});
            skLineSegment(sketch, "E81", {"start": v(15, 120) * mm, "end": v(15, 108) * mm});
            skLineSegment(sketch, "E82", {"start": v(15, 108) * mm, "end": v(33, 90) * mm});
            skLineSegment(sketch, "E83", {"start": v(-15, 120) * mm, "end": v(-15, 108) * mm});
            skLineSegment(sketch, "E84", {"start": v(-15, 108) * mm, "end": v(-33, 90) * mm});
            skArc(sketch, "E85", {"start": v(15, 120) * mm, "mid": v(0, 135) * mm, "end": v(-15, 120) * mm});
            skLineSegment(sketch, "E86", {"start": v(80, 0) * mm, "end": v(-80, 0) * mm, "construction": true});
            skLineSegment(sketch, "E87.MirrorCS", {"start": v(15, -120) * mm, "end": v(15, -108) * mm});
            skLineSegment(sketch, "E88.MirrorCS", {"start": v(-15, -120) * mm, "end": v(-15, -108) * mm});
            skArc(sketch, "E89.MirrorCS", {"start": v(15, -120) * mm, "mid": v(0, -135) * mm, "end": v(-15, -120) * mm});
            skCircle(sketch, "E90.MirrorC", {"center": v(0, -120) * mm, "radius": 6 * mm});
            skLineSegment(sketch, "E91.MirrorCS", {"start": v(15, -108) * mm, "end": v(33, -90) * mm});
            skLineSegment(sketch, "E92.MirrorCS", {"start": v(-15, -108) * mm, "end": v(-33, -90) * mm});
            skSolve(sketch);
        }
        {
            var Q0;
            Q0=makeQuery(id+"F16.imprint","IMPRINT",FACE,{"disambiguationData":[TD([[makeQuery(id+"F16.imprint","IMPRINT",EDGE,{"derivedFrom":sQuery(id+"F16.wireOp",EDGE,"E87.MirrorCS")}),1.0]])]});
            var Q1;
            Q1=makeQuery(id+"F16.imprint","IMPRINT",FACE,{"disambiguationData":[TD([[makeQuery(id+"F16.imprint","IMPRINT",EDGE,{"derivedFrom":makeQuery(id+"F1.opExtrude","CAP_EDGE",EDGE,{"disambiguationData":[OSD([sQuery(id+"F0.wireOp",EDGE,"E1.left")])],"isStart":true})}),-1.0]])]});
            var Q2;
            Q2=makeQuery(id+"F16.imprint","IMPRINT",FACE,{"disambiguationData":[TD([[makeQuery(id+"F16.imprint","IMPRINT",EDGE,{"derivedFrom":sQuery(id+"F16.wireOp",EDGE,"E80")}),-1.0]])]});
            var Q3;
            Q3=makeQuery(id+"F2.opExtrude","CAP_FACE",FACE,{"disambiguationData":[OSD([sQuery(id+"F0.wireOp",EDGE,"E12"),sQuery(id+"F0.wireOp",EDGE,"E13"),sQuery(id+"F0.wireOp",EDGE,"E14"),sQuery(id+"F0.wireOp",EDGE,"E15"),sQuery(id+"F0.wireOp",EDGE,"E17.filletArc"),sQuery(id+"F0.wireOp",EDGE,"E18.filletArc"),sQuery(id+"F0.wireOp",EDGE,"E19.filletArc"),sQuery(id+"F0.wireOp",EDGE,"E20.filletArc"),sQuery(id+"F0.wireOp",EDGE,"E25.0"),sQuery(id+"F0.wireOp",EDGE,"E25.1"),sQuery(id+"F0.wireOp",EDGE,"E25.2"),sQuery(id+"F0.wireOp",EDGE,"E25.3"),sQuery(id+"F0.wireOp",EDGE,"E25.4"),sQuery(id+"F0.wireOp",EDGE,"E25.5"),sQuery(id+"F0.wireOp",EDGE,"E25.6"),sQuery(id+"F0.wireOp",EDGE,"E25.7")])],"isStart":false});
            extrude(context, id + "F17", {"entities" : qUnion([Q0, Q1, Q2]), "endBound" : BoundingType.UP_TO_SURFACE, "endBoundEntityFace" : qUnion([Q3]), "depth" : 25 * mm});
        }
    });
